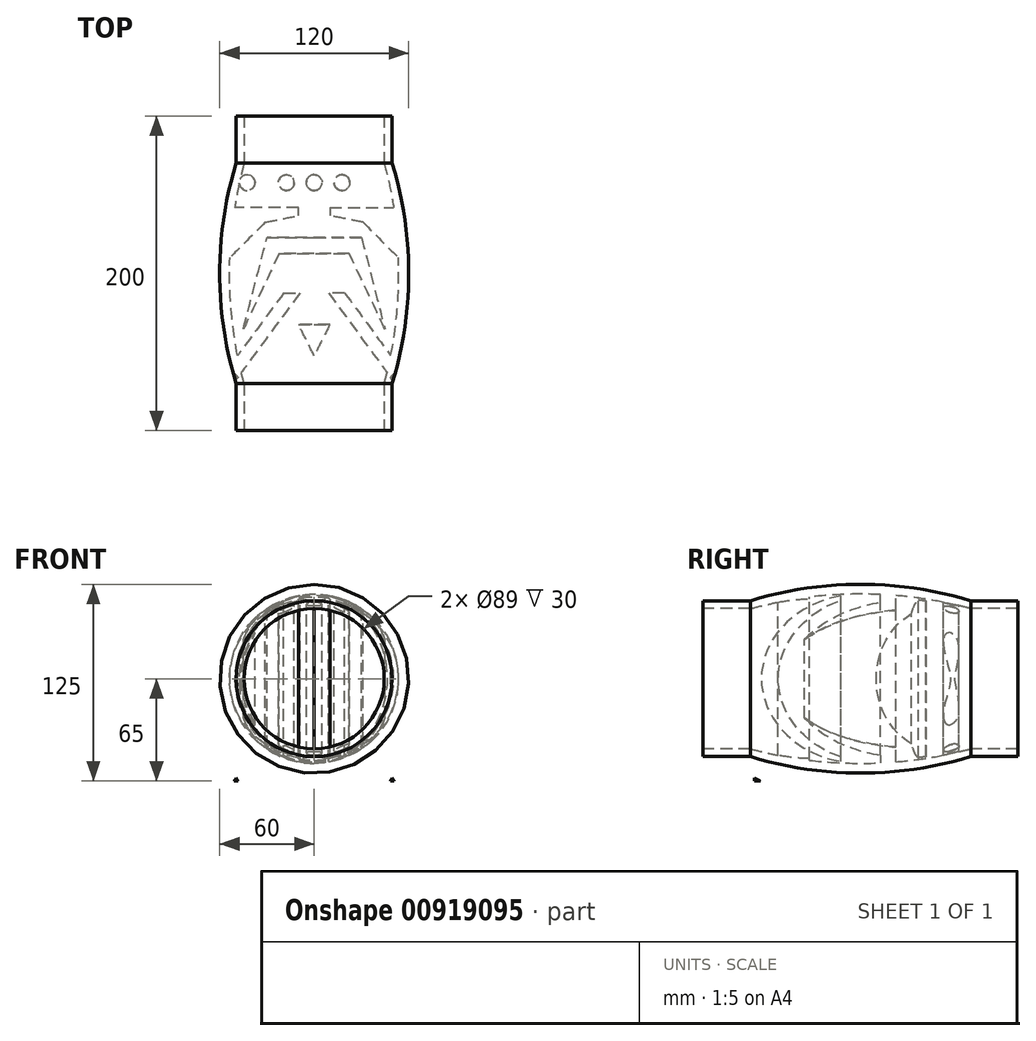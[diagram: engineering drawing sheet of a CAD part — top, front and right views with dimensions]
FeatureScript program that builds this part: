
annotation { "Feature Type Name" : "Feature", "Feature Type Description" : "" }
export const myFeature = defineFeature(function(context is Context, id is Id, definition is map)
    precondition{}
    {
        {
            var Q0;
            Q0=qCreatedBy(makeId("Top.planeOp"),FACE);
            var sketch = newSketch(context, id + "F0", { "sketchPlane" : qUnion([Q0])});
            skLineSegment(sketch, "E0", {"start": v(0, 130.65) * mm, "end": v(0, -163.78) * mm});
            skLineSegment(sketch, "E1", {"start": v(-49.5, -88.7) * mm, "end": v(-49.5, -58.7) * mm});
            skLineSegment(sketch, "E2", {"start": v(-49.5, 111.3) * mm, "end": v(-49.5, 81.3) * mm});
            skArc(sketch, "E3", {"start": v(-49.5, 81.3) * mm, "mid": v(-60, 11.3) * mm, "end": v(-49.5, -58.7) * mm});
            skLineSegment(sketch, "E4", {"start": v(-49.5, 111.3) * mm, "end": v(0, 111.3) * mm});
            skLineSegment(sketch, "E5", {"start": v(0, 111.3) * mm, "end": v(0, -88.7) * mm});
            skLineSegment(sketch, "E6", {"start": v(0, -88.7) * mm, "end": v(-49.5, -88.7) * mm});
            skLineSegment(sketch, "E7", {"start": v(-49.5, -88.7) * mm, "end": v(-78.46, -88.7) * mm});
            skLineSegment(sketch, "E8", {"start": v(-78.46, -88.7) * mm, "end": v(-78.46, -58.7) * mm});
            skLineSegment(sketch, "E9", {"start": v(-78.46, 111.3) * mm, "end": v(-78.46, 81.3) * mm});
            skLineSegment(sketch, "E10", {"start": v(-78.46, 111.3) * mm, "end": v(-49.5, 111.3) * mm});
            skArc(sketch, "E11", {"start": v(-78.46, 81.3) * mm, "mid": v(-100, 11.3) * mm, "end": v(-78.46, -58.7) * mm});
            skSolve(sketch);
        }
        {
            var Q0;
            Q0=qCreatedBy(makeId("Top.planeOp"),FACE);
            cPlane(context, id + "F1", {"entities" : qUnion([Q0]), "cplaneType" : CPlaneType.OFFSET, "offset" : 60 * mm, "width" : 150 * mm, "height" : 150 * mm});
        }
        {
            var Q0;
            Q0=qCreatedBy(id+"F1.planeOp",FACE);
            var sketch = newSketch(context, id + "F2", { "sketchPlane" : qUnion([Q0])});
            skLineSegment(sketch, "E12", {"start": v(-30, 33.9) * mm, "end": v(30, 33.9) * mm});
            skLineSegment(sketch, "E13", {"start": v(30, 33.9) * mm, "end": v(45, -24.2) * mm});
            skLineSegment(sketch, "E14", {"start": v(45, -24.2) * mm, "end": v(22.25, 23.9) * mm});
            skLineSegment(sketch, "E15", {"start": v(22.25, 23.9) * mm, "end": v(-22.25, 23.9) * mm});
            skLineSegment(sketch, "E16", {"start": v(-22.25, 23.9) * mm, "end": v(-45, -24.2) * mm});
            skLineSegment(sketch, "E17", {"start": v(-45, -24.2) * mm, "end": v(-30, 33.9) * mm});
            skPoint(sketch, "E18.startSnap0", {"position": v(-35.43, 83.9) * mm});
            skLineSegment(sketch, "E19", {"start": v(-60, 117.58) * mm, "end": v(-60, -108.72) * mm});
            skLineSegment(sketch, "E20", {"start": v(60, 120.37) * mm, "end": v(60, -108.32) * mm});
            skLineSegment(sketch, "E21", {"start": v(-124.3, -56.1) * mm, "end": v(135.05, -56.1) * mm});
            skLineSegment(sketch, "E22", {"start": v(-89.01, 83.9) * mm, "end": v(152.85, 83.9) * mm});
            skSolve(sketch);
        }
        {
            var Q0;
            Q0=qCreatedBy(id+"F1.planeOp",FACE);
            var sketch = newSketch(context, id + "F3", { "sketchPlane" : qUnion([Q0])});
            skLineSegment(sketch, "E23", {"start": v(-49.5, -56.1) * mm, "end": v(-9.05, -1.1) * mm});
            skLineSegment(sketch, "E24", {"start": v(-9.05, -1.1) * mm, "end": v(-19.32, -1.1) * mm});
            skLineSegment(sketch, "E25", {"start": v(-19.32, -1.1) * mm, "end": v(-52.85, -46.68) * mm});
            skLineSegment(sketch, "E26", {"start": v(-52.85, -46.68) * mm, "end": v(-49.5, -56.1) * mm});
            skLineSegment(sketch, "E27.MirrorCS", {"start": v(49.5, -56.1) * mm, "end": v(9.05, -1.1) * mm});
            skLineSegment(sketch, "E28.MirrorCS", {"start": v(19.32, -1.1) * mm, "end": v(52.85, -46.68) * mm});
            skLineSegment(sketch, "E29.MirrorCS", {"start": v(9.05, -1.1) * mm, "end": v(19.32, -1.1) * mm});
            skLineSegment(sketch, "E30.MirrorCS", {"start": v(52.85, -46.68) * mm, "end": v(49.5, -56.1) * mm});
            skSolve(sketch);
        }
        {
            var Q0;
            Q0=qCreatedBy(id+"F1.planeOp",FACE);
            var sketch = newSketch(context, id + "F4", { "sketchPlane" : qUnion([Q0])});
            skLineSegment(sketch, "E31", {"start": v(-10, -21.1) * mm, "end": v(10, -21.1) * mm});
            skLineSegment(sketch, "E32", {"start": v(10, -21.1) * mm, "end": v(0, -41.1) * mm});
            skLineSegment(sketch, "E33", {"start": v(0, -41.1) * mm, "end": v(-10, -21.1) * mm});
            skSolve(sketch);
        }
        {
            var Q0;
            Q0=qCreatedBy(id+"F1.planeOp",FACE);
            var sketch = newSketch(context, id + "F5", { "sketchPlane" : qUnion([Q0])});
            skLineSegment(sketch, "E34", {"start": v(-35, 52.93) * mm, "end": v(-10, 52.93) * mm});
            skLineSegment(sketch, "E35", {"start": v(-10, 52.93) * mm, "end": v(-10, 47.93) * mm});
            skLineSegment(sketch, "E36", {"start": v(-10, 47.93) * mm, "end": v(-31.06, 43.74) * mm});
            skLineSegment(sketch, "E37", {"start": v(-31.06, 43.74) * mm, "end": v(-60, 14.73) * mm});
            skLineSegment(sketch, "E38", {"start": v(-35, 52.93) * mm, "end": v(-56.34, 52.93) * mm});
            skLineSegment(sketch, "E39", {"start": v(-56.34, 52.93) * mm, "end": v(-60, 14.73) * mm});
            skLineSegment(sketch, "E40.MirrorCS", {"start": v(35, 52.93) * mm, "end": v(56.34, 52.93) * mm});
            skLineSegment(sketch, "E41.MirrorCS", {"start": v(35, 52.93) * mm, "end": v(10, 52.93) * mm});
            skLineSegment(sketch, "E42.MirrorCS", {"start": v(10, 52.93) * mm, "end": v(10, 47.93) * mm});
            skLineSegment(sketch, "E43.MirrorCS", {"start": v(10, 47.93) * mm, "end": v(31.06, 43.74) * mm});
            skLineSegment(sketch, "E44.MirrorCS", {"start": v(31.06, 43.74) * mm, "end": v(60, 14.73) * mm});
            skLineSegment(sketch, "E45.MirrorCS", {"start": v(56.34, 52.93) * mm, "end": v(60, 14.73) * mm});
            skSolve(sketch);
        }
        {
            var Q0;
            Q0=qCreatedBy(id+"F1.planeOp",FACE);
            var sketch = newSketch(context, id + "F6", { "sketchPlane" : qUnion([Q0])});
            skCircle(sketch, "E46", {"center": v(-42.63, 68.9) * mm, "radius": 5 * mm});
            skCircle(sketch, "E47", {"center": v(-17.63, 68.9) * mm, "radius": 5 * mm});
            skCircle(sketch, "E48", {"center": v(0, 68.9) * mm, "radius": 5 * mm});
            skLineSegment(sketch, "E49", {"start": v(-73.25, 68.9) * mm, "end": v(101.38, 68.9) * mm});
            skCircle(sketch, "E50.MirrorC", {"center": v(17.63, 68.9) * mm, "radius": 5 * mm});
            skCircle(sketch, "E51.MirrorC", {"center": v(42.63, 68.9) * mm, "radius": 5 * mm});
            skSolve(sketch);
        }
        {
            var Q0;
            Q0=qCreatedBy(makeId("Top.planeOp"),FACE);
            var sketch = newSketch(context, id + "F7", { "sketchPlane" : qUnion([Q0])});
            skLineSegment(sketch, "E52", {"start": v(0, 111.3) * mm, "end": v(-44.5, 111.3) * mm});
            skLineSegment(sketch, "E53", {"start": v(-44.5, 111.3) * mm, "end": v(-44.5, 81.3) * mm});
            skLineSegment(sketch, "E54", {"start": v(-44.5, -58.7) * mm, "end": v(-44.5, -88.7) * mm});
            skLineSegment(sketch, "E55", {"start": v(-44.5, -88.7) * mm, "end": v(0, -88.7) * mm});
            skLineSegment(sketch, "E56", {"start": v(0, -88.7) * mm, "end": v(0, 111.3) * mm});
            skArc(sketch, "E57", {"start": v(-44.5, 81.3) * mm, "mid": v(-53.73, 11.3) * mm, "end": v(-44.5, -58.7) * mm});
            skSolve(sketch);
        }
        {
            var Q0;
            Q0=makeQuery(id+"F0.imprint","IMPRINT",FACE,{"disambiguationData":[TD([[makeQuery(id+"F0.imprint","IMPRINT",EDGE,{"derivedFrom":sQuery(id+"F0.wireOp",EDGE,"E4")}),-1.0]])]});
            var Q1;
            Q1=sQuery(id+"F0.wireOp",EDGE,"E0");
            revolve(context, id + "F8", {"surfaceOperationType" : NewSurfaceOperationType.NEW, "entities" : qUnion([Q0]), "axis" : qUnion([Q1]), "revolveType" : RevolveType.FULL});
        }
        {
            var Q0;
            Q0 = qSketchRegion(id + "F7", true);
            var Q1;
            Q1=sQuery(id+"F0.wireOp",EDGE,"E0");
            revolve(context, id + "F9", {"operationType" : NewBodyOperationType.REMOVE, "surfaceOperationType" : NewSurfaceOperationType.NEW, "entities" : qUnion([Q0]), "axis" : qUnion([Q1]), "revolveType" : RevolveType.FULL, "oppositeDirection" : true});
        }
        {
            var Q0;
            Q0=makeQuery(id+"F2.imprint","IMPRINT",FACE,{"disambiguationData":[TD([[makeQuery(id+"F2.imprint","IMPRINT",EDGE,{"derivedFrom":sQuery(id+"F2.wireOp",EDGE,"E12")}),-1.0]])]});
            var Q1;
            Q1=makeQuery(id+"F5.imprint","IMPRINT",FACE,{"disambiguationData":[TD([[makeQuery(id+"F5.imprint","IMPRINT",EDGE,{"derivedFrom":sQuery(id+"F5.wireOp",EDGE,"E40.MirrorCS")}),-1.0]])]});
            var Q2;
            Q2=makeQuery(id+"F5.imprint","IMPRINT",FACE,{"disambiguationData":[TD([[makeQuery(id+"F5.imprint","IMPRINT",EDGE,{"derivedFrom":sQuery(id+"F5.wireOp",EDGE,"E34")}),-1.0]])]});
            var Q3;
            Q3=makeQuery(id+"F3.imprint","IMPRINT",FACE,{"disambiguationData":[TD([[makeQuery(id+"F3.imprint","IMPRINT",EDGE,{"derivedFrom":sQuery(id+"F3.wireOp",EDGE,"E23")}),1.0]])]});
            var Q4;
            Q4=makeQuery(id+"F4.imprint","IMPRINT",FACE,{"disambiguationData":[TD([[makeQuery(id+"F4.imprint","IMPRINT",EDGE,{"derivedFrom":sQuery(id+"F4.wireOp",EDGE,"E31")}),-1.0]])]});
            var Q5;
            Q5=makeQuery(id+"F3.imprint","IMPRINT",FACE,{"disambiguationData":[TD([[makeQuery(id+"F3.imprint","IMPRINT",EDGE,{"derivedFrom":sQuery(id+"F3.wireOp",EDGE,"E27.MirrorCS")}),-1.0]])]});
            var Q6;
            {var subQ0=sQuery(id+"F6.wireOp",EDGE,"E51.MirrorC");var subQ1=sQuery(id+"F6.wireOp",EDGE,"E49");var subQ2=makeQuery(id+"F6.imprint","INTERSECT",VERTEX,{"disambiguationData":[OD(0.0)],"derivedFrom":[subQ1,subQ0]});Q6=makeQuery(id+"F6.imprint","IMPRINT",FACE,{"disambiguationData":[TD([[makeQuery(id+"F6.imprint","IMPRINT",EDGE,{"disambiguationData":[TD([[subQ2,-1.0]])],"derivedFrom":subQ1}),-1.0]])]});}
            var Q7;
            {var subQ0=sQuery(id+"F6.wireOp",EDGE,"E51.MirrorC");var subQ1=sQuery(id+"F6.wireOp",EDGE,"E49");var subQ2=makeQuery(id+"F6.imprint","INTERSECT",VERTEX,{"disambiguationData":[OD(0.0)],"derivedFrom":[subQ1,subQ0]});Q7=makeQuery(id+"F6.imprint","IMPRINT",FACE,{"disambiguationData":[TD([[makeQuery(id+"F6.imprint","IMPRINT",EDGE,{"disambiguationData":[TD([[subQ2,-1.0]])],"derivedFrom":subQ1}),1.0]])]});}
            var Q8;
            {var subQ0=sQuery(id+"F6.wireOp",EDGE,"E50.MirrorC");var subQ1=sQuery(id+"F6.wireOp",EDGE,"E49");var subQ2=makeQuery(id+"F6.imprint","INTERSECT",VERTEX,{"disambiguationData":[OD(0.0)],"derivedFrom":[subQ1,subQ0]});Q8=makeQuery(id+"F6.imprint","IMPRINT",FACE,{"disambiguationData":[TD([[makeQuery(id+"F6.imprint","IMPRINT",EDGE,{"disambiguationData":[TD([[subQ2,-1.0]])],"derivedFrom":subQ1}),1.0]])]});}
            var Q9;
            {var subQ0=sQuery(id+"F6.wireOp",EDGE,"E50.MirrorC");var subQ1=sQuery(id+"F6.wireOp",EDGE,"E49");var subQ2=makeQuery(id+"F6.imprint","INTERSECT",VERTEX,{"disambiguationData":[OD(0.0)],"derivedFrom":[subQ1,subQ0]});Q9=makeQuery(id+"F6.imprint","IMPRINT",FACE,{"disambiguationData":[TD([[makeQuery(id+"F6.imprint","IMPRINT",EDGE,{"disambiguationData":[TD([[subQ2,-1.0]])],"derivedFrom":subQ1}),-1.0]])]});}
            var Q10;
            {var subQ0=sQuery(id+"F6.wireOp",EDGE,"E49");var subQ1=sQuery(id+"F6.wireOp",EDGE,"E48");var subQ2=makeQuery(id+"F6.imprint","INTERSECT",VERTEX,{"disambiguationData":[OD(0.0)],"derivedFrom":[subQ1,subQ0]});Q10=makeQuery(id+"F6.imprint","IMPRINT",FACE,{"disambiguationData":[TD([[makeQuery(id+"F6.imprint","IMPRINT",EDGE,{"disambiguationData":[TD([[subQ2,1.0]])],"derivedFrom":subQ1}),1.0]])]});}
            var Q11;
            {var subQ0=sQuery(id+"F6.wireOp",EDGE,"E49");var subQ1=sQuery(id+"F6.wireOp",EDGE,"E47");var subQ2=makeQuery(id+"F6.imprint","INTERSECT",VERTEX,{"disambiguationData":[OD(0.0)],"derivedFrom":[subQ1,subQ0]});Q11=makeQuery(id+"F6.imprint","IMPRINT",FACE,{"disambiguationData":[TD([[makeQuery(id+"F6.imprint","IMPRINT",EDGE,{"disambiguationData":[TD([[subQ2,1.0]])],"derivedFrom":subQ1}),1.0]])]});}
            var Q12;
            {var subQ0=sQuery(id+"F6.wireOp",EDGE,"E49");var subQ1=sQuery(id+"F6.wireOp",EDGE,"E47");var subQ2=makeQuery(id+"F6.imprint","INTERSECT",VERTEX,{"disambiguationData":[OD(0.0)],"derivedFrom":[subQ1,subQ0]});Q12=makeQuery(id+"F6.imprint","IMPRINT",FACE,{"disambiguationData":[TD([[makeQuery(id+"F6.imprint","IMPRINT",EDGE,{"disambiguationData":[TD([[subQ2,-1.0]])],"derivedFrom":subQ1}),1.0]])]});}
            var Q13;
            {var subQ0=sQuery(id+"F6.wireOp",EDGE,"E49");var subQ1=sQuery(id+"F6.wireOp",EDGE,"E46");var subQ2=makeQuery(id+"F6.imprint","INTERSECT",VERTEX,{"disambiguationData":[OD(0.0)],"derivedFrom":[subQ1,subQ0]});Q13=makeQuery(id+"F6.imprint","IMPRINT",FACE,{"disambiguationData":[TD([[makeQuery(id+"F6.imprint","IMPRINT",EDGE,{"disambiguationData":[TD([[subQ2,1.0]])],"derivedFrom":subQ1}),1.0]])]});}
            var Q14;
            {var subQ0=sQuery(id+"F6.wireOp",EDGE,"E49");var subQ1=sQuery(id+"F6.wireOp",EDGE,"E46");var subQ2=makeQuery(id+"F6.imprint","INTERSECT",VERTEX,{"disambiguationData":[OD(0.0)],"derivedFrom":[subQ1,subQ0]});Q14=makeQuery(id+"F6.imprint","IMPRINT",FACE,{"disambiguationData":[TD([[makeQuery(id+"F6.imprint","IMPRINT",EDGE,{"disambiguationData":[TD([[subQ2,-1.0]])],"derivedFrom":subQ1}),1.0]])]});}
            var Q15;
            {var subQ0=sQuery(id+"F6.wireOp",EDGE,"E49");var subQ1=sQuery(id+"F6.wireOp",EDGE,"E48");var subQ2=makeQuery(id+"F6.imprint","INTERSECT",VERTEX,{"disambiguationData":[OD(0.0)],"derivedFrom":[subQ1,subQ0]});Q15=makeQuery(id+"F6.imprint","IMPRINT",FACE,{"disambiguationData":[TD([[makeQuery(id+"F6.imprint","IMPRINT",EDGE,{"disambiguationData":[TD([[subQ2,-1.0]])],"derivedFrom":subQ1}),1.0]])]});}
            extrude(context, id + "F10", {"entities" : qUnion([Q0, Q1, Q2, Q3, Q4, Q5, Q6, Q7, Q8, Q9, Q10, Q11, Q12, Q13, Q14, Q15]), "operationType" : NewBodyOperationType.ADD, "oppositeDirection" : true, "depth" : 125 * mm, "offsetDistance" : 25 * mm});
        }
        {
            var Q0;
            {var subQ0=sQuery(id+"F5.wireOp",EDGE,"E41.MirrorCS");var subQ1=sQuery(id+"F5.wireOp",EDGE,"E40.MirrorCS");var subQ2=sQuery(id+"F5.wireOp",EDGE,"E42.MirrorCS");Q0=makeQuery(id+"F10.boolean.opBoolean","SPLIT",EDGE,{"disambiguationData":[TD([makeQuery(id+"F10.opExtrude","CAP_FACE",FACE,{"disambiguationData":[OSD([subQ1,subQ0,subQ2,sQuery(id+"F5.wireOp",EDGE,"E43.MirrorCS"),sQuery(id+"F5.wireOp",EDGE,"E44.MirrorCS"),sQuery(id+"F5.wireOp",EDGE,"E45.MirrorCS")])],"isStart":true})])],"derivedFrom":makeQuery(id+"F10.opExtrude","SWEPT_EDGE",EDGE,{"disambiguationData":[OSD([subQ0,subQ2])]})});}
            var Q1;
            {var subQ0=sQuery(id+"F5.wireOp",EDGE,"E43.MirrorCS");var subQ1=sQuery(id+"F5.wireOp",EDGE,"E42.MirrorCS");Q1=makeQuery(id+"F10.boolean.opBoolean","SPLIT",EDGE,{"disambiguationData":[TD([makeQuery(id+"F10.opExtrude","CAP_FACE",FACE,{"disambiguationData":[OSD([sQuery(id+"F5.wireOp",EDGE,"E40.MirrorCS"),sQuery(id+"F5.wireOp",EDGE,"E41.MirrorCS"),subQ1,subQ0,sQuery(id+"F5.wireOp",EDGE,"E44.MirrorCS"),sQuery(id+"F5.wireOp",EDGE,"E45.MirrorCS")])],"isStart":true})])],"derivedFrom":makeQuery(id+"F10.opExtrude","SWEPT_EDGE",EDGE,{"disambiguationData":[OSD([subQ1,subQ0])]})});}
            var Q2;
            {var subQ0=sQuery(id+"F5.wireOp",EDGE,"E36");var subQ1=sQuery(id+"F5.wireOp",EDGE,"E35");Q2=makeQuery(id+"F10.boolean.opBoolean","SPLIT",EDGE,{"disambiguationData":[TD([makeQuery(id+"F10.opExtrude","CAP_FACE",FACE,{"disambiguationData":[OSD([sQuery(id+"F5.wireOp",EDGE,"E34"),subQ1,subQ0,sQuery(id+"F5.wireOp",EDGE,"E37"),sQuery(id+"F5.wireOp",EDGE,"E38"),sQuery(id+"F5.wireOp",EDGE,"E39")])],"isStart":true})])],"derivedFrom":makeQuery(id+"F10.opExtrude","SWEPT_EDGE",EDGE,{"disambiguationData":[OSD([subQ1,subQ0])]})});}
            var Q3;
            {var subQ0=sQuery(id+"F5.wireOp",EDGE,"E38");var subQ1=sQuery(id+"F5.wireOp",EDGE,"E35");var subQ2=sQuery(id+"F5.wireOp",EDGE,"E34");Q3=makeQuery(id+"F10.boolean.opBoolean","SPLIT",EDGE,{"disambiguationData":[TD([makeQuery(id+"F10.opExtrude","CAP_FACE",FACE,{"disambiguationData":[OSD([subQ2,subQ1,sQuery(id+"F5.wireOp",EDGE,"E36"),sQuery(id+"F5.wireOp",EDGE,"E37"),subQ0,sQuery(id+"F5.wireOp",EDGE,"E39")])],"isStart":true})])],"derivedFrom":makeQuery(id+"F10.opExtrude","SWEPT_EDGE",EDGE,{"disambiguationData":[OSD([subQ2,subQ1])]})});}
            var Q4;
            {var subQ0=sQuery(id+"F2.wireOp",EDGE,"E17");var subQ1=sQuery(id+"F2.wireOp",EDGE,"E12");Q4=makeQuery(id+"F10.boolean.opBoolean","SPLIT",EDGE,{"disambiguationData":[TD([makeQuery(id+"F10.opExtrude","CAP_FACE",FACE,{"disambiguationData":[OSD([subQ1,sQuery(id+"F2.wireOp",EDGE,"E13"),sQuery(id+"F2.wireOp",EDGE,"E14"),sQuery(id+"F2.wireOp",EDGE,"E15"),sQuery(id+"F2.wireOp",EDGE,"E16"),subQ0])],"isStart":true})])],"derivedFrom":makeQuery(id+"F10.opExtrude","SWEPT_EDGE",EDGE,{"disambiguationData":[OSD([subQ1,subQ0])]})});}
            var Q5;
            {var subQ0=sQuery(id+"F2.wireOp",EDGE,"E13");var subQ1=sQuery(id+"F2.wireOp",EDGE,"E12");Q5=makeQuery(id+"F10.boolean.opBoolean","SPLIT",EDGE,{"disambiguationData":[TD([makeQuery(id+"F10.opExtrude","CAP_FACE",FACE,{"disambiguationData":[OSD([subQ1,subQ0,sQuery(id+"F2.wireOp",EDGE,"E14"),sQuery(id+"F2.wireOp",EDGE,"E15"),sQuery(id+"F2.wireOp",EDGE,"E16"),sQuery(id+"F2.wireOp",EDGE,"E17")])],"isStart":true})])],"derivedFrom":makeQuery(id+"F10.opExtrude","SWEPT_EDGE",EDGE,{"disambiguationData":[OSD([subQ1,subQ0])]})});}
            var Q6;
            {var subQ0=sQuery(id+"F3.wireOp",EDGE,"E29.MirrorCS");var subQ1=sQuery(id+"F3.wireOp",EDGE,"E28.MirrorCS");Q6=makeQuery(id+"F10.boolean.opBoolean","SPLIT",EDGE,{"disambiguationData":[TD([makeQuery(id+"F10.opExtrude","CAP_FACE",FACE,{"disambiguationData":[OSD([sQuery(id+"F3.wireOp",EDGE,"E27.MirrorCS"),subQ1,subQ0,sQuery(id+"F3.wireOp",EDGE,"E30.MirrorCS")])],"isStart":true})])],"derivedFrom":makeQuery(id+"F10.opExtrude","SWEPT_EDGE",EDGE,{"disambiguationData":[OSD([subQ1,subQ0])]})});}
            var Q7;
            {var subQ0=sQuery(id+"F3.wireOp",EDGE,"E27.MirrorCS");var subQ1=sQuery(id+"F3.wireOp",EDGE,"E29.MirrorCS");Q7=makeQuery(id+"F10.boolean.opBoolean","SPLIT",EDGE,{"disambiguationData":[TD([makeQuery(id+"F10.opExtrude","CAP_FACE",FACE,{"disambiguationData":[OSD([subQ0,sQuery(id+"F3.wireOp",EDGE,"E28.MirrorCS"),subQ1,sQuery(id+"F3.wireOp",EDGE,"E30.MirrorCS")])],"isStart":true})])],"derivedFrom":makeQuery(id+"F10.opExtrude","SWEPT_EDGE",EDGE,{"disambiguationData":[OSD([subQ0,subQ1])]})});}
            var Q8;
            {var subQ0=sQuery(id+"F3.wireOp",EDGE,"E24");var subQ1=sQuery(id+"F3.wireOp",EDGE,"E23");Q8=makeQuery(id+"F10.boolean.opBoolean","SPLIT",EDGE,{"disambiguationData":[TD([makeQuery(id+"F10.opExtrude","CAP_FACE",FACE,{"disambiguationData":[OSD([subQ1,subQ0,sQuery(id+"F3.wireOp",EDGE,"E25"),sQuery(id+"F3.wireOp",EDGE,"E26")])],"isStart":true})])],"derivedFrom":makeQuery(id+"F10.opExtrude","SWEPT_EDGE",EDGE,{"disambiguationData":[OSD([subQ1,subQ0])]})});}
            var Q9;
            {var subQ0=sQuery(id+"F3.wireOp",EDGE,"E24");var subQ1=sQuery(id+"F3.wireOp",EDGE,"E25");Q9=makeQuery(id+"F10.boolean.opBoolean","SPLIT",EDGE,{"disambiguationData":[TD([makeQuery(id+"F10.opExtrude","CAP_FACE",FACE,{"disambiguationData":[OSD([sQuery(id+"F3.wireOp",EDGE,"E23"),subQ0,subQ1,sQuery(id+"F3.wireOp",EDGE,"E26")])],"isStart":true})])],"derivedFrom":makeQuery(id+"F10.opExtrude","SWEPT_EDGE",EDGE,{"disambiguationData":[OSD([subQ0,subQ1])]})});}
            var Q10;
            {var subQ0=sQuery(id+"F4.wireOp",EDGE,"E33");var subQ1=sQuery(id+"F4.wireOp",EDGE,"E31");Q10=makeQuery(id+"F10.boolean.opBoolean","SPLIT",EDGE,{"disambiguationData":[TD([makeQuery(id+"F10.opExtrude","CAP_FACE",FACE,{"disambiguationData":[OSD([subQ1,sQuery(id+"F4.wireOp",EDGE,"E32"),subQ0])],"isStart":true})])],"derivedFrom":makeQuery(id+"F10.opExtrude","SWEPT_EDGE",EDGE,{"disambiguationData":[OSD([subQ1,subQ0])]})});}
            var Q11;
            {var subQ0=sQuery(id+"F4.wireOp",EDGE,"E32");var subQ1=sQuery(id+"F4.wireOp",EDGE,"E31");Q11=makeQuery(id+"F10.boolean.opBoolean","SPLIT",EDGE,{"disambiguationData":[TD([makeQuery(id+"F10.opExtrude","CAP_FACE",FACE,{"disambiguationData":[OSD([subQ1,subQ0,sQuery(id+"F4.wireOp",EDGE,"E33")])],"isStart":true})])],"derivedFrom":makeQuery(id+"F10.opExtrude","SWEPT_EDGE",EDGE,{"disambiguationData":[OSD([subQ1,subQ0])]})});}
            var Q12;
            {var subQ0=sQuery(id+"F2.wireOp",EDGE,"E14");var subQ1=sQuery(id+"F2.wireOp",EDGE,"E13");Q12=makeQuery(id+"F10.boolean.opBoolean","SPLIT",EDGE,{"disambiguationData":[TD([makeQuery(id+"F10.opExtrude","CAP_FACE",FACE,{"disambiguationData":[OSD([sQuery(id+"F2.wireOp",EDGE,"E12"),subQ1,subQ0,sQuery(id+"F2.wireOp",EDGE,"E15"),sQuery(id+"F2.wireOp",EDGE,"E16"),sQuery(id+"F2.wireOp",EDGE,"E17")])],"isStart":true})])],"derivedFrom":makeQuery(id+"F10.opExtrude","SWEPT_EDGE",EDGE,{"disambiguationData":[OSD([subQ1,subQ0])]})});}
            var Q13;
            {var subQ0=sQuery(id+"F2.wireOp",EDGE,"E17");var subQ1=sQuery(id+"F2.wireOp",EDGE,"E16");Q13=makeQuery(id+"F10.boolean.opBoolean","SPLIT",EDGE,{"disambiguationData":[TD([makeQuery(id+"F10.opExtrude","CAP_FACE",FACE,{"disambiguationData":[OSD([sQuery(id+"F2.wireOp",EDGE,"E12"),sQuery(id+"F2.wireOp",EDGE,"E13"),sQuery(id+"F2.wireOp",EDGE,"E14"),sQuery(id+"F2.wireOp",EDGE,"E15"),subQ1,subQ0])],"isStart":true})])],"derivedFrom":makeQuery(id+"F10.opExtrude","SWEPT_EDGE",EDGE,{"disambiguationData":[OSD([subQ1,subQ0])]})});}
            fillet(context, id + "F11", {"entities" : qUnion([Q0, Q1, Q2, Q3, Q4, Q5, Q6, Q7, Q8, Q9, Q10, Q11, Q12, Q13]), "radius" : 2 * mm, "tangentPropagation" : true, "allowEdgeOverflow" : false});
        }
        {
            var Q0;
            {var subQ0=sQuery(id+"F5.wireOp",EDGE,"E37");var subQ1=sQuery(id+"F5.wireOp",EDGE,"E36");Q0=makeQuery(id+"F10.boolean.opBoolean","SPLIT",EDGE,{"disambiguationData":[TD([makeQuery(id+"F10.opExtrude","CAP_FACE",FACE,{"disambiguationData":[OSD([sQuery(id+"F5.wireOp",EDGE,"E34"),sQuery(id+"F5.wireOp",EDGE,"E35"),subQ1,subQ0,sQuery(id+"F5.wireOp",EDGE,"E38"),sQuery(id+"F5.wireOp",EDGE,"E39")])],"isStart":true})])],"derivedFrom":makeQuery(id+"F10.opExtrude","SWEPT_EDGE",EDGE,{"disambiguationData":[OSD([subQ1,subQ0])]})});}
            var Q1;
            {var subQ0=sQuery(id+"F2.wireOp",EDGE,"E16");var subQ1=sQuery(id+"F2.wireOp",EDGE,"E15");Q1=makeQuery(id+"F10.boolean.opBoolean","SPLIT",EDGE,{"disambiguationData":[TD([makeQuery(id+"F10.opExtrude","CAP_FACE",FACE,{"disambiguationData":[OSD([sQuery(id+"F2.wireOp",EDGE,"E12"),sQuery(id+"F2.wireOp",EDGE,"E13"),sQuery(id+"F2.wireOp",EDGE,"E14"),subQ1,subQ0,sQuery(id+"F2.wireOp",EDGE,"E17")])],"isStart":true})])],"derivedFrom":makeQuery(id+"F10.opExtrude","SWEPT_EDGE",EDGE,{"disambiguationData":[OSD([subQ1,subQ0])]})});}
            var Q2;
            {var subQ0=sQuery(id+"F2.wireOp",EDGE,"E15");var subQ1=sQuery(id+"F2.wireOp",EDGE,"E14");Q2=makeQuery(id+"F10.boolean.opBoolean","SPLIT",EDGE,{"disambiguationData":[TD([makeQuery(id+"F10.opExtrude","CAP_FACE",FACE,{"disambiguationData":[OSD([sQuery(id+"F2.wireOp",EDGE,"E12"),sQuery(id+"F2.wireOp",EDGE,"E13"),subQ1,subQ0,sQuery(id+"F2.wireOp",EDGE,"E16"),sQuery(id+"F2.wireOp",EDGE,"E17")])],"isStart":true})])],"derivedFrom":makeQuery(id+"F10.opExtrude","SWEPT_EDGE",EDGE,{"disambiguationData":[OSD([subQ1,subQ0])]})});}
            var Q3;
            {var subQ0=sQuery(id+"F5.wireOp",EDGE,"E43.MirrorCS");var subQ1=sQuery(id+"F5.wireOp",EDGE,"E44.MirrorCS");Q3=makeQuery(id+"F10.boolean.opBoolean","SPLIT",EDGE,{"disambiguationData":[TD([makeQuery(id+"F10.opExtrude","CAP_FACE",FACE,{"disambiguationData":[OSD([sQuery(id+"F5.wireOp",EDGE,"E40.MirrorCS"),sQuery(id+"F5.wireOp",EDGE,"E41.MirrorCS"),sQuery(id+"F5.wireOp",EDGE,"E42.MirrorCS"),subQ0,subQ1,sQuery(id+"F5.wireOp",EDGE,"E45.MirrorCS")])],"isStart":true})])],"derivedFrom":makeQuery(id+"F10.opExtrude","SWEPT_EDGE",EDGE,{"disambiguationData":[OSD([subQ0,subQ1])]})});}
            fillet(context, id + "F12", {"entities" : qUnion([Q0, Q1, Q2, Q3]), "radius" : 10 * mm, "tangentPropagation" : true, "allowEdgeOverflow" : false});
        }
        {
            var Q0;
            Q0=makeQuery(id+"F0.imprint","IMPRINT",FACE,{"disambiguationData":[TD([[makeQuery(id+"F0.imprint","IMPRINT",EDGE,{"derivedFrom":sQuery(id+"F0.wireOp",EDGE,"E1")}),1.0]])]});
            var Q1;
            Q1=sQuery(id+"F0.wireOp",EDGE,"E0");
            revolve(context, id + "F13", {"operationType" : NewBodyOperationType.REMOVE, "surfaceOperationType" : NewSurfaceOperationType.NEW, "entities" : qUnion([Q0]), "axis" : qUnion([Q1]), "revolveType" : RevolveType.FULL, "oppositeDirection" : true});
        }
    });
